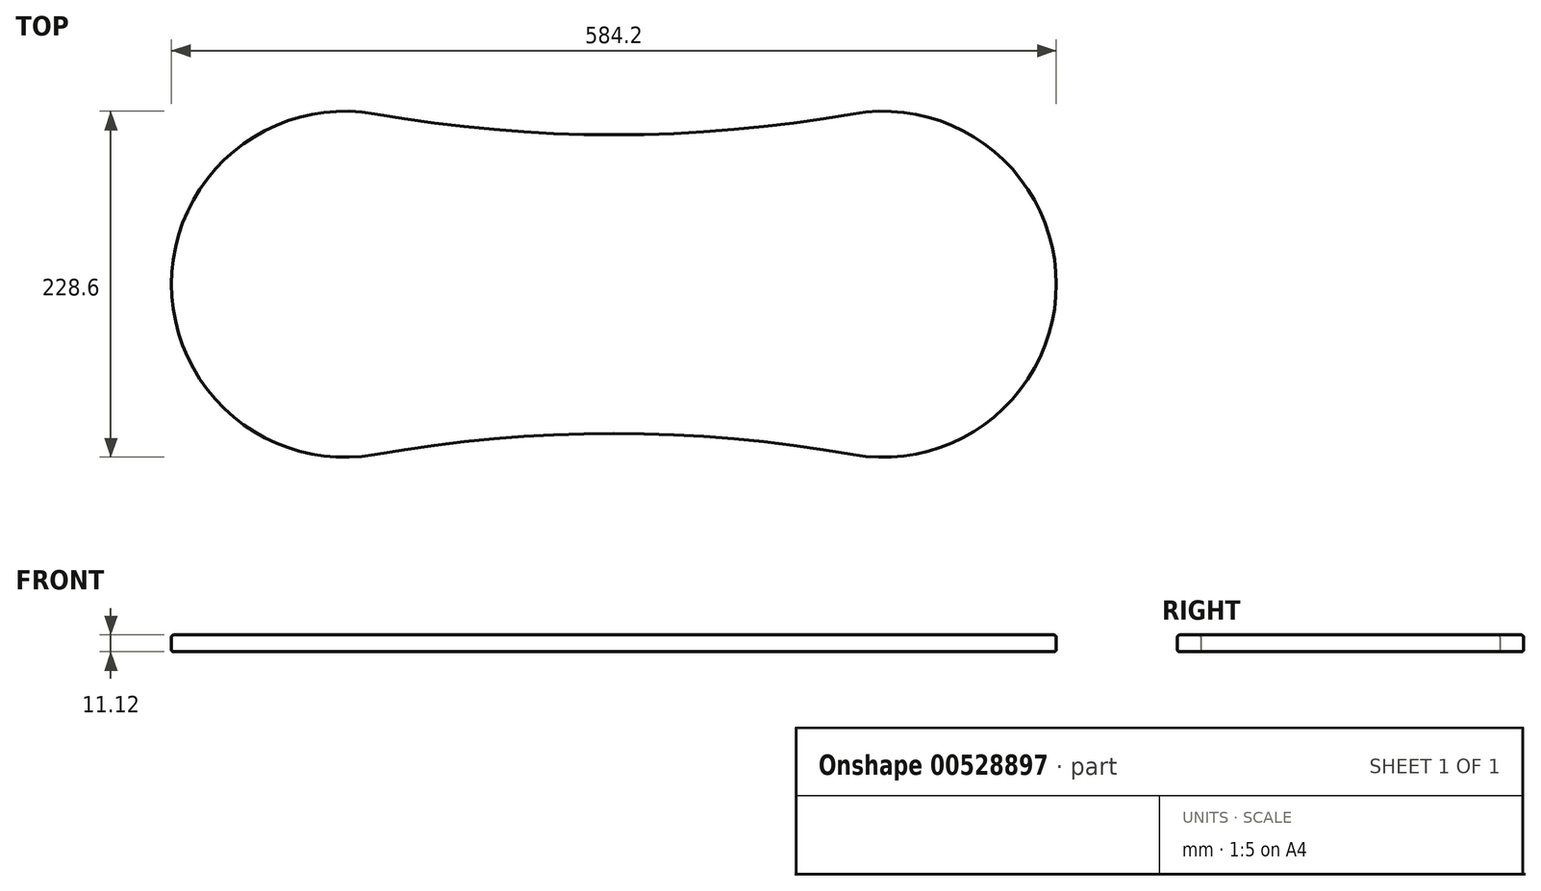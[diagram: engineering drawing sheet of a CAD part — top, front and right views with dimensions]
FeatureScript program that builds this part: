
annotation { "Feature Type Name" : "Feature", "Feature Type Description" : "" }
export const myFeature = defineFeature(function(context is Context, id is Id, definition is map)
    precondition{}
    {
        {
            var Q0;
            Q0=qCreatedBy(makeId("Top.planeOp"),FACE);
            var sketch = newSketch(context, id + "F0", { "sketchPlane" : qUnion([Q0])});
            skPoint(sketch, "E0.middle", {"position": v(0, 0) * mm});
            skArc(sketch, "E1", {"start": v(-177.8, 114.3) * mm, "mid": v(-292.1, 0) * mm, "end": v(-177.8, -114.3) * mm});
            skArc(sketch, "E2", {"start": v(177.8, -114.3) * mm, "mid": v(292.1, 0) * mm, "end": v(177.8, 114.3) * mm});
            skArc(sketch, "E3", {"start": v(-177.8, 114.3) * mm, "mid": v(-167.84, 113.87) * mm, "end": v(-157.95, 112.56) * mm});
            skArc(sketch, "E4", {"start": v(177.8, 114.3) * mm, "mid": v(167.84, 113.87) * mm, "end": v(157.95, 112.56) * mm});
            skArc(sketch, "E5", {"start": v(-157.95, 112.56) * mm, "mid": v(0, 98.74) * mm, "end": v(157.95, 112.56) * mm});
            skArc(sketch, "E6", {"start": v(-177.8, -114.3) * mm, "mid": v(-167.84, -113.87) * mm, "end": v(-157.95, -112.56) * mm});
            skArc(sketch, "E7", {"start": v(177.8, -114.3) * mm, "mid": v(167.84, -113.87) * mm, "end": v(157.95, -112.56) * mm});
            skArc(sketch, "E8", {"start": v(-157.95, -112.56) * mm, "mid": v(0, -98.74) * mm, "end": v(157.95, -112.56) * mm});
            skSolve(sketch);
        }
        {
            var Q0;
            Q0=makeQuery(id+"F0.imprint","IMPRINT",FACE,{"disambiguationData":[TD([[makeQuery(id+"F0.imprint","IMPRINT",EDGE,{"derivedFrom":sQuery(id+"F0.wireOp",EDGE,"E1")}),1.0]])]});
            extrude(context, id + "F1", {"entities" : qUnion([Q0]), "endBound" : BoundingType.SYMMETRIC, "depth" : 11.1 * mm, "offsetDistance" : 25.4 * mm});
        }
        {
            var Q0;
            Q0=makeQuery(id+"F1.opExtrude","CAP_FACE",FACE,{"disambiguationData":[OSD([sQuery(id+"F0.wireOp",EDGE,"E1"),sQuery(id+"F0.wireOp",EDGE,"E2"),sQuery(id+"F0.wireOp",EDGE,"E3"),sQuery(id+"F0.wireOp",EDGE,"E4"),sQuery(id+"F0.wireOp",EDGE,"E5"),sQuery(id+"F0.wireOp",EDGE,"E6"),sQuery(id+"F0.wireOp",EDGE,"E7"),sQuery(id+"F0.wireOp",EDGE,"E8")])],"isStart":false});
            var Q1;
            Q1=makeQuery(id+"F1.opExtrude","CAP_FACE",FACE,{"disambiguationData":[OSD([sQuery(id+"F0.wireOp",EDGE,"E1"),sQuery(id+"F0.wireOp",EDGE,"E2"),sQuery(id+"F0.wireOp",EDGE,"E3"),sQuery(id+"F0.wireOp",EDGE,"E4"),sQuery(id+"F0.wireOp",EDGE,"E5"),sQuery(id+"F0.wireOp",EDGE,"E6"),sQuery(id+"F0.wireOp",EDGE,"E7"),sQuery(id+"F0.wireOp",EDGE,"E8")])],"isStart":true});
            fillet(context, id + "F2", {"entities" : qUnion([Q0, Q1]), "radius" : 1.59 * mm, "tangentPropagation" : true, "allowEdgeOverflow" : false});
        }
    });
